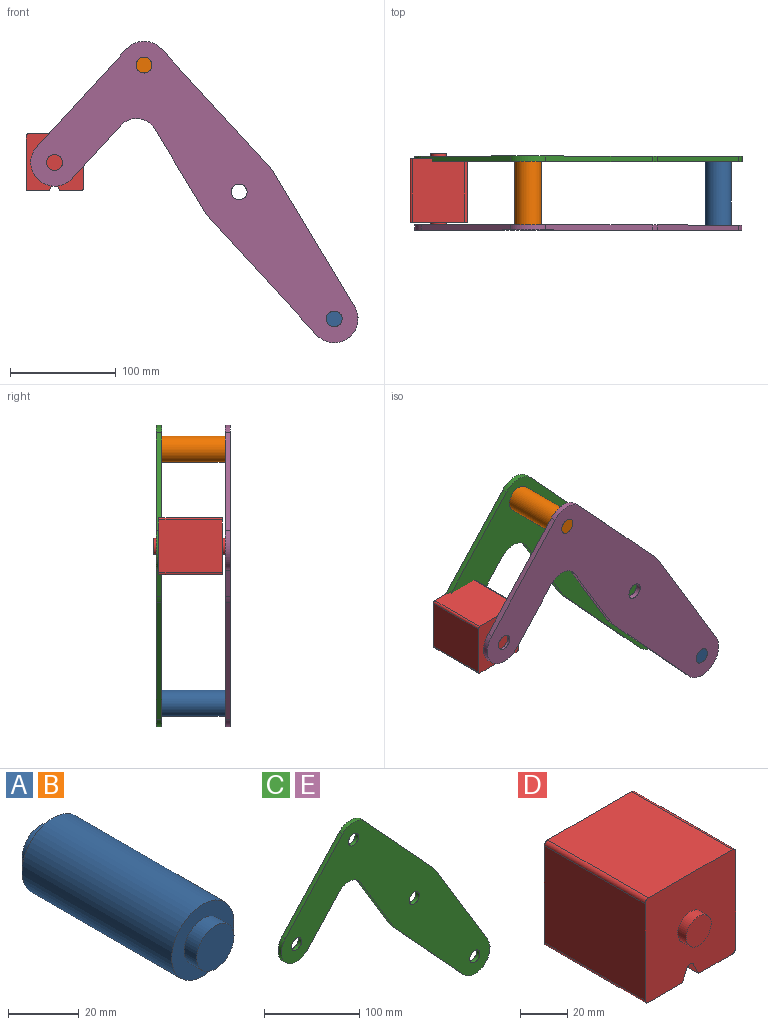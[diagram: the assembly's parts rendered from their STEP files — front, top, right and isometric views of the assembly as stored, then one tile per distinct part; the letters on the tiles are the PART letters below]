
ASSEMBLY  parts=5 mates=3
PART A: 7 faces, bbox 25x70x25 mm
  f0: cylinder r=12.5mm len=60mm, axis (0,-1,0), area 4712.4mm2, adj f2,f5
  f1: cylinder r=7.5mm len=15mm, axis (0,1,0), area 235.6mm2, adj f2,f3
  f2: plane 25x25mm, normal (0,-1,0), area 314.2mm2, adj f0,f1
  f3: plane 15x15mm, normal (0,-1,0), area 176.7mm2, adj f1
  f4: cylinder r=7.5mm len=15mm, axis (0,-1,0), area 235.6mm2, adj f5,f6
  f5: plane 25x25mm, normal (0,1,0), area 314.2mm2, adj f0,f4
  f6: plane 15x15mm, normal (0,1,0), area 176.7mm2, adj f4
PART B: same geometry as A
PART C: 18 faces, bbox 309.5x5x285.1 mm
  f0: cylinder r=22.5mm len=39.07mm, axis (0,1,0), area 353.4mm2, adj f1,f13,f16,f17
  f1: plane 50.28x46.21mm, normal (0.74,0,-0.68), area 341.4mm2, adj f0,f2,f16,f17
  f2: cylinder r=20mm len=31.85mm, axis (0,1,0), area 185.5mm2, adj f1,f3,f16,f17
  f3: plane 79.23x47.81mm, normal (-0.86,0,-0.52), area 462.7mm2, adj f2,f4,f16,f17
  f4: cylinder r=37.5mm len=6mm, axis (0,1,0), area 37.6mm2, adj f3,f5,f16,f17
  f5: plane 109.88x101mm, normal (-0.74,0,-0.68), area 746.2mm2, adj f4,f6,f16,f17
  f6: cylinder r=22.5mm len=39.07mm, axis (0,1,0), area 330.9mm2, adj f5,f7,f16,f17
  f7: plane 127.78x77.11mm, normal (0.86,0,0.52), area 746.2mm2, adj f6,f8,f16,f17
  f8: cylinder r=37.5mm len=6mm, axis (0,1,0), area 37.6mm2, adj f7,f9,f16,f17
  f9: plane 109.88x101mm, normal (0.74,0,0.68), area 746.2mm2, adj f8,f10,f16,f17
  f10: cylinder r=22.5mm len=33.13mm, axis (0,1,0), area 186.2mm2, adj f9,f13,f16,f17
  f11: cylinder r=7.5mm len=15mm, axis (0,1,0), area 235.6mm2, adj f16,f17
  f12: cylinder r=7.5mm len=15mm, axis (0,1,0), area 235.6mm2, adj f16,f17
  f13: plane 92.03x84.59mm, normal (-0.74,0,0.68), area 625mm2, adj f0,f10,f16,f17
  f14: cylinder r=7.5mm len=15mm, axis (0,1,0), area 235.6mm2, adj f16,f17
  f15: cylinder r=7.5mm len=15mm, axis (0,1,0), area 235.6mm2, adj f16,f17
  f16: plane 309.5x285.07mm, normal (0,-1,0), area 24555.4mm2, adj f0,f1,f2,f3,f4,f5,f6,f7
  f17: plane 309.5x285.07mm, normal (0,1,0), area 24555.4mm2, adj f0,f1,f2,f3,f4,f5,f6,f7
PART D: 18 faces, bbox 54x70x54 mm
  f0: plane 60x50.01mm, normal (0,0,1), area 3000.4mm2, adj f4,f10,f13,f14
  f1: plane 60x50.01mm, normal (-1,0,0), area 3000.4mm2, adj f4,f10,f14,f15
  f2: plane 60x20mm, normal (0,0,-1), area 1200.2mm2, adj f3,f4,f10,f15
  f3: plane 60x6.42mm, normal (0.89,0,-0.45), area 430.8mm2, adj f2,f4,f10,f16
  f4: plane 54.01x54.01mm, normal (0,-1,0), area 2690.1mm2, adj f0,f1,f2,f3,f5,f6,f7,f9
  f5: plane 60x50.01mm, normal (1,0,0), area 3000.4mm2, adj f4,f10,f13,f17
  f6: plane 60x6.42mm, normal (-0.89,0,-0.45), area 430.8mm2, adj f4,f7,f10,f16
  f7: plane 60x20mm, normal (0,0,-1), area 1200.2mm2, adj f4,f6,f10,f17
  f8: plane 15x15mm, normal (0,-1,0), area 176.7mm2, adj f9
  f9: cylinder r=7.5mm len=15mm, axis (0,1,0), area 235.6mm2, adj f4,f8
  f10: plane 54.01x54.01mm, normal (0,1,0), area 2690.1mm2, adj f0,f1,f2,f3,f5,f6,f7,f12
  f11: plane 15x15mm, normal (0,1,0), area 176.7mm2, adj f12
  f12: cylinder r=7.5mm len=15mm, axis (0,-1,0), area 235.6mm2, adj f10,f11
  f13: cylinder r=2mm len=60mm, axis (0,-1,0), area 188.5mm2, adj f0,f4,f5,f10
  f14: cylinder r=2mm len=60mm, axis (0,1,0), area 188.5mm2, adj f0,f1,f4,f10
  f15: cylinder r=2mm len=60mm, axis (0,-1,0), area 188.5mm2, adj f1,f2,f4,f10
  f16: cylinder r=2mm len=60mm, axis (0,-1,0), area 265.7mm2, adj f3,f4,f6,f10
  f17: cylinder r=2mm len=60mm, axis (0,1,0), area 188.5mm2, adj f4,f5,f7,f10
PART E: same geometry as C
PLACE A t=(179.91,-30,-240.07)mm
PLACE B t=(0,-30,0)mm
PLACE C t=(0,35,0)mm
PLACE D t=(0,-27.5,0)mm
PLACE E t=(0,-30,0)mm fixed
MATE fastened B.f0 <-> C.f10  axis (0,1,0) through (-89.96,30,120.03)mm
MATE fastened A.f0 <-> E.f6  axis (0,-1,0) through (89.96,-30,-120.03)mm
MATE revolute E.f0 <-> D.f9  axis (0,1,0) through (-174.54,-30,28)mm
